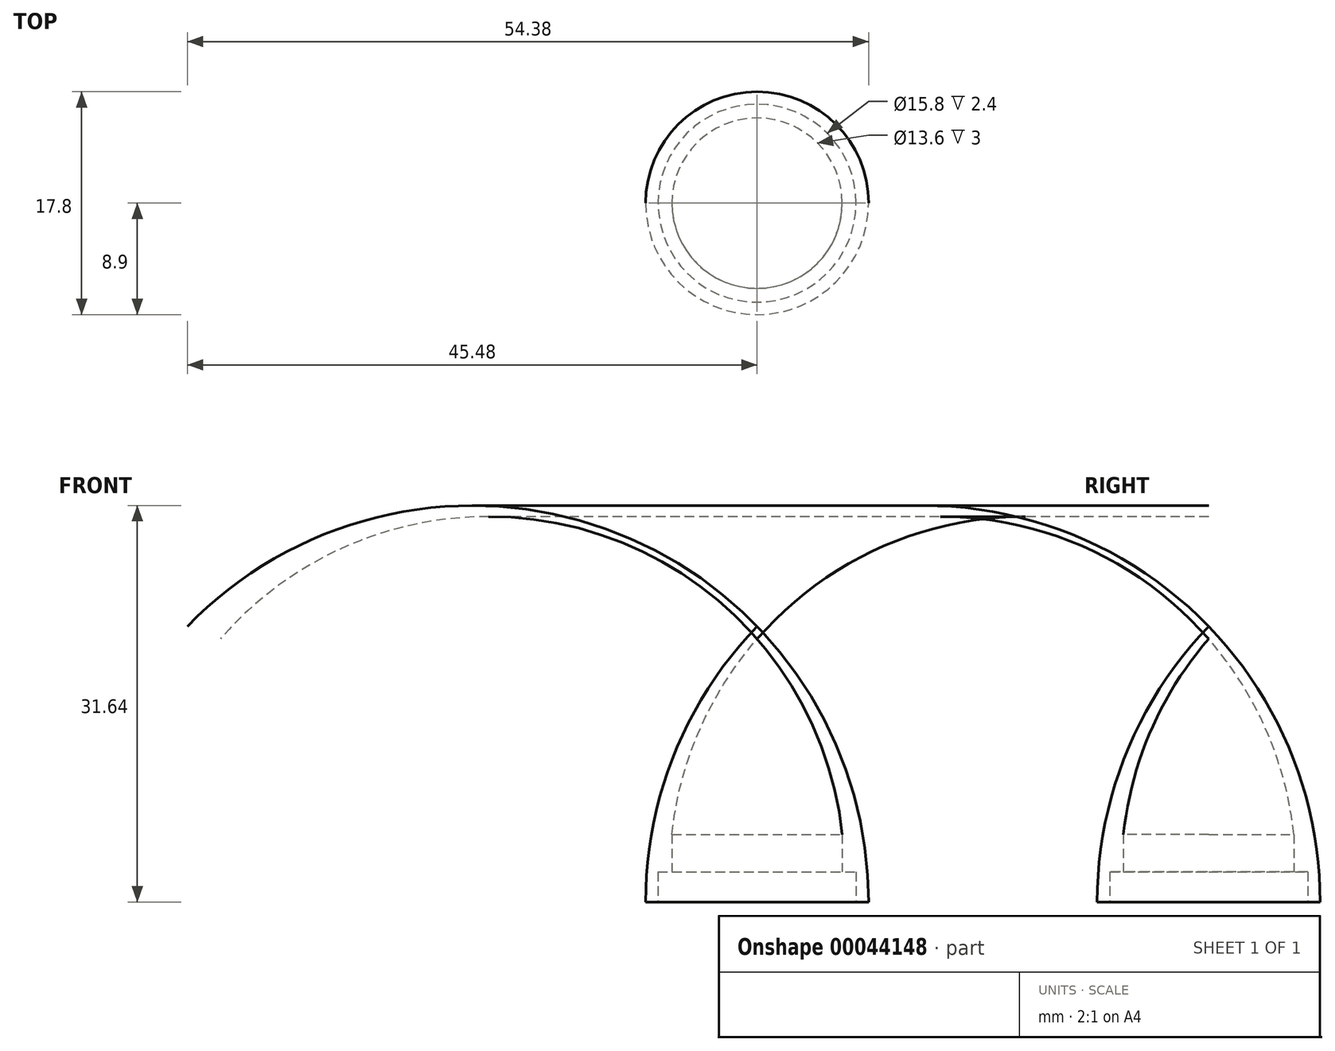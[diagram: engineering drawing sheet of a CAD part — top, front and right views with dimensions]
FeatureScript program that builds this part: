
annotation { "Feature Type Name" : "Feature", "Feature Type Description" : "" }
export const myFeature = defineFeature(function(context is Context, id is Id, definition is map)
    precondition{}
    {
        {
            var Q0;
            Q0=qCreatedBy(makeId("Top.planeOp"),FACE);
            var sketch = newSketch(context, id + "F0", { "sketchPlane" : qUnion([Q0])});
            skLineSegment(sketch, "E0", {"start": v(-17.52, 0) * mm, "end": v(42.68, 0) * mm, "construction": true});
            skLineSegment(sketch, "E1", {"start": v(0, 0) * mm, "end": v(0, 7.9) * mm, "construction": true});
            skLineSegment(sketch, "E2", {"start": v(0, 7.9) * mm, "end": v(2.4, 7.9) * mm});
            skLineSegment(sketch, "E3", {"start": v(2.4, 6.8) * mm, "end": v(2.4, 7.9) * mm});
            skLineSegment(sketch, "E4", {"start": v(2.4, 6.8) * mm, "end": v(5.4, 6.8) * mm});
            skLineSegment(sketch, "E5", {"start": v(0, 7.9) * mm, "end": v(0, 8.9) * mm});
            skArc(sketch, "E6", {"start": v(22, 0) * mm, "mid": v(11.87, 6.6) * mm, "end": v(0, 8.9) * mm});
            skArc(sketch, "E7", {"start": v(21, 0) * mm, "mid": v(13.72, 4.6) * mm, "end": v(5.4, 6.8) * mm});
            skLineSegment(sketch, "E8", {"start": v(21, 0) * mm, "end": v(22, 0) * mm});
            skSolve(sketch);
        }
        {
            var Q0;
            Q0=makeQuery(id+"F0.imprint","IMPRINT",FACE,{"disambiguationData":[TD([[makeQuery(id+"F0.imprint","IMPRINT",EDGE,{"derivedFrom":sQuery(id+"F0.wireOp",EDGE,"E2")}),1.0]])]});
            var Q1;
            Q1=sQuery(id+"F0.wireOp",EDGE,"E0");
            revolve(context, id + "F1", {"entities" : qUnion([Q0]), "axis" : qUnion([Q1]), "revolveType" : RevolveType.FULL});
        }
        {
            var Q0;
            Q0=qCreatedBy(makeId("Front.planeOp"),FACE);
            var sketch = newSketch(context, id + "F2", { "sketchPlane" : qUnion([Q0])});
            skCircle(sketch, "E9", {"center": v(0, 0) * mm, "radius": 5.7 * mm});
            skSolve(sketch);
        }
        {
            var Q0;
            Q0=makeQuery(id+"F1.opRevolve","SWEPT_BODY",BODY,{"disambiguationData":[OSD([sQuery(id+"F0.wireOp",EDGE,"E2"),sQuery(id+"F0.wireOp",EDGE,"E3"),sQuery(id+"F0.wireOp",EDGE,"E4"),sQuery(id+"F0.wireOp",EDGE,"E5"),sQuery(id+"F0.wireOp",EDGE,"E6"),sQuery(id+"F0.wireOp",EDGE,"E7"),sQuery(id+"F0.wireOp",EDGE,"E8")])]});
            var Q1;
            Q1=sQuery(id+"F2.wireOp",EDGE,"E9");
            transform(context, id + "F3", {"entities" : qUnion([Q0]), "transformType" : TransformType.ROTATION, "transformAxis" : qUnion([Q1]), "angle" : 90 * degree, "makeCopy" : false});
        }
    });
